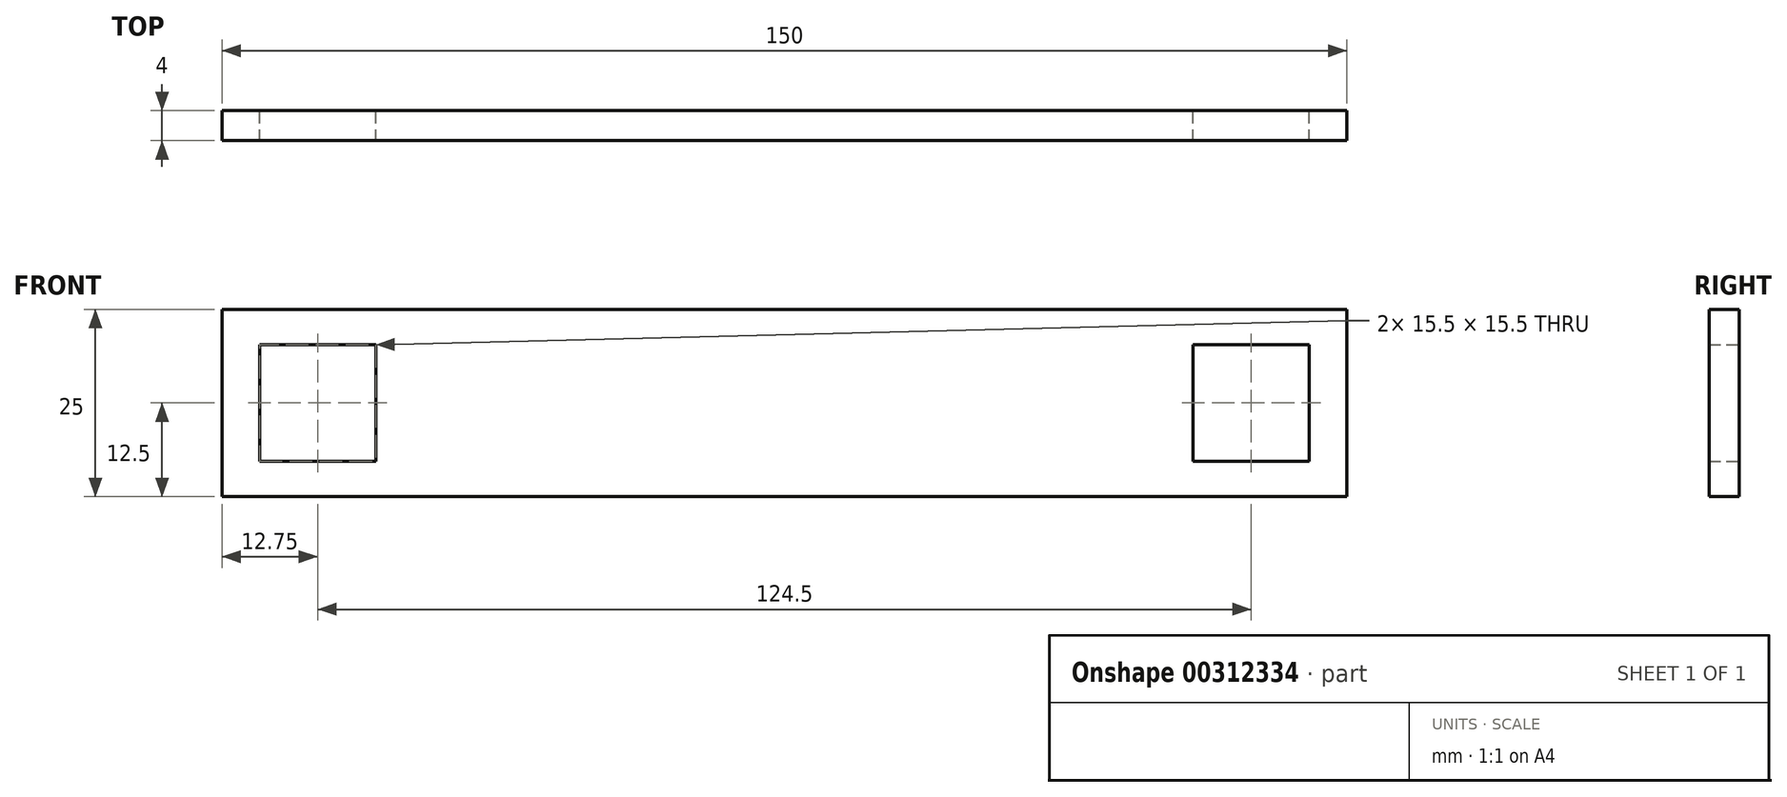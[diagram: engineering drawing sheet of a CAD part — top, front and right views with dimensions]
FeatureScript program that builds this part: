
annotation { "Feature Type Name" : "Feature", "Feature Type Description" : "" }
export const myFeature = defineFeature(function(context is Context, id is Id, definition is map)
    precondition{}
    {
        {
            var Q0;
            Q0=qCreatedBy(makeId("Front.planeOp"),FACE);
            var sketch = newSketch(context, id + "F0", { "sketchPlane" : qUnion([Q0])});
            skLineSegment(sketch, "E0.bottom", {"start": v(7.75, 7.75) * mm, "end": v(-7.75, 7.75) * mm});
            skLineSegment(sketch, "E0.top", {"start": v(7.75, -7.75) * mm, "end": v(-7.75, -7.75) * mm});
            skLineSegment(sketch, "E0.left", {"start": v(7.75, 7.75) * mm, "end": v(7.75, -7.75) * mm});
            skLineSegment(sketch, "E0.right", {"start": v(-7.75, 7.75) * mm, "end": v(-7.75, -7.75) * mm});
            skPoint(sketch, "E0.middle", {"position": v(0, 0) * mm});
            skLineSegment(sketch, "E1", {"start": v(7.75, 0) * mm, "end": v(12.75, 0) * mm});
            skPoint(sketch, "E1.endSnap0", {"position": v(7.75, 0) * mm});
            skLineSegment(sketch, "E2", {"start": v(12.75, 0) * mm, "end": v(12.75, 12.5) * mm});
            skLineSegment(sketch, "E3", {"start": v(12.75, 0) * mm, "end": v(12.75, -12.5) * mm});
            skLineSegment(sketch, "E4", {"start": v(12.75, 12.5) * mm, "end": v(-137.25, 12.5) * mm});
            skLineSegment(sketch, "E5", {"start": v(-137.25, 12.5) * mm, "end": v(-137.25, -12.5) * mm});
            skLineSegment(sketch, "E6", {"start": v(-137.25, -12.5) * mm, "end": v(12.75, -12.5) * mm});
            skLineSegment(sketch, "E7", {"start": v(-62.25, 12.5) * mm, "end": v(-62.25, -15.57) * mm, "construction": true});
            skPoint(sketch, "E7.endSnap0", {"position": v(-62.25, 12.5) * mm});
            skLineSegment(sketch, "E8.MirrorCS", {"start": v(-132.25, 7.75) * mm, "end": v(-116.75, 7.75) * mm});
            skLineSegment(sketch, "E9.MirrorCS", {"start": v(-116.75, 7.75) * mm, "end": v(-116.75, -7.75) * mm});
            skLineSegment(sketch, "E10.MirrorCS", {"start": v(-132.25, 7.75) * mm, "end": v(-132.25, -7.75) * mm});
            skLineSegment(sketch, "E11.MirrorCS", {"start": v(-132.25, -7.75) * mm, "end": v(-116.75, -7.75) * mm});
            skSolve(sketch);
        }
        {
            var Q0;
            {var subQ0=sQuery(id+"F0.wireOp",EDGE,"E0.bottom");Q0=makeQuery(id+"F0.imprint","IMPRINT",FACE,{"disambiguationData":[TD([[makeQuery(id+"F0.imprint","IMPRINT",EDGE,{"derivedFrom":subQ0}),-1.0]])]});}
            extrude(context, id + "F1", {"entities" : qUnion([Q0]), "depth" : 4 * mm});
        }
    });
